# Revit family: Geberit VariForm yuvarlak tezgah üstü lavabo_PRO_1833148
name_source: partatom
category: Plumbing Fixtures
revit_build: Autodesk Revit 2018 (Build: 20190510_1515(x64)
units: mm (PartAtom-declared; Revit-internal decimal feet)

## family parameters
Always vertical = Yes
Cut with Voids When Loaded = No
OmniClass Number = 23.45.05.21
OmniClass Title = Plumbing Fixtures - Sanitary Disposal Units
Part Type = Normal
Room Calculation Point = Yes
Round Connector Dimension = Use Diameter
Shared = No
Work Plane-Based = No

## types (2) — shared parameters
500700_0_view = Yes
Application purposes = Tezgah üstlerine üstten montaj için
Application range = Plumbing fixture
BIM Content Version = GEB MG 1.2
BIM Content revision date = 2020.05.18
Brand = Geberit
CW Connection = Yes
Characteristics = Yuvarlak
Birlikte verilen kesit şablonu sayesinde kolay montaj
Description = Geberit VariForm yuvarlak tezgah üstü lavabo
GEB_culture = tr-TR
GEB_generic_description = Bathroom collection
GEB_generic_manufacturer = generic
GEB_pimversion = 22.02.12
GEB_processing_type = T
GEB_reference = PRO_1833148
GEB_translations = {"ATT_10673":"EAN code basic data","ATT_10882":"Malzeme","ATT_459792":"Renk / Yüzey","applicationPurposes":"Application purposes","application_range":"Application range","brandName":"Brand","characteristics":"Characteristics","content_creator":"BIM Content creator","content_date_changed":"BIM Content revision date","content_version":"BIM Content Version","key 1000":"Article number key","name":"Name","productBrand":"Product brand","scopeOfDelivery":"Scope of delivery","type":"Type","fixed_material":"Main material"}
HW Connection = No
IfcDescription = Geberit VariForm yuvarlak tezgah üstü lavabo
IfcExportAs = IfcSanitaryTerminal
IfcExportType = WASHHANDBASIN
LOD300 = No
LOD400 = Yes
Main material = Geberit, Plastic, Opaque white
Malzeme = Seramik
Manufacturer = Geberit
Name = Geberit VariForm yuvarlak tezgah üstü lavabo
Renk / Yüzey = Beyaz
Scope of delivery = Şablon
Vent Connection = No
Waste Connection = Yes
outlet_flow = 0.0 L/s

## per-type parameters (varying)
| type | Article number key | EAN code basic data |
| 500.700.01.2 Geberit VariForm yuvarlak tezgah üstü lavabo | 500.700.01.2 | 4025416823414 |
| 500.702.01.2 Geberit VariForm yuvarlak tezgah üstü lavabo | 500.702.01.2 | 4025416824732 |

## geometry (parser evidence)
native form markers: Blend x8, Sweep x13
no freeform markers — native parametric forms only
